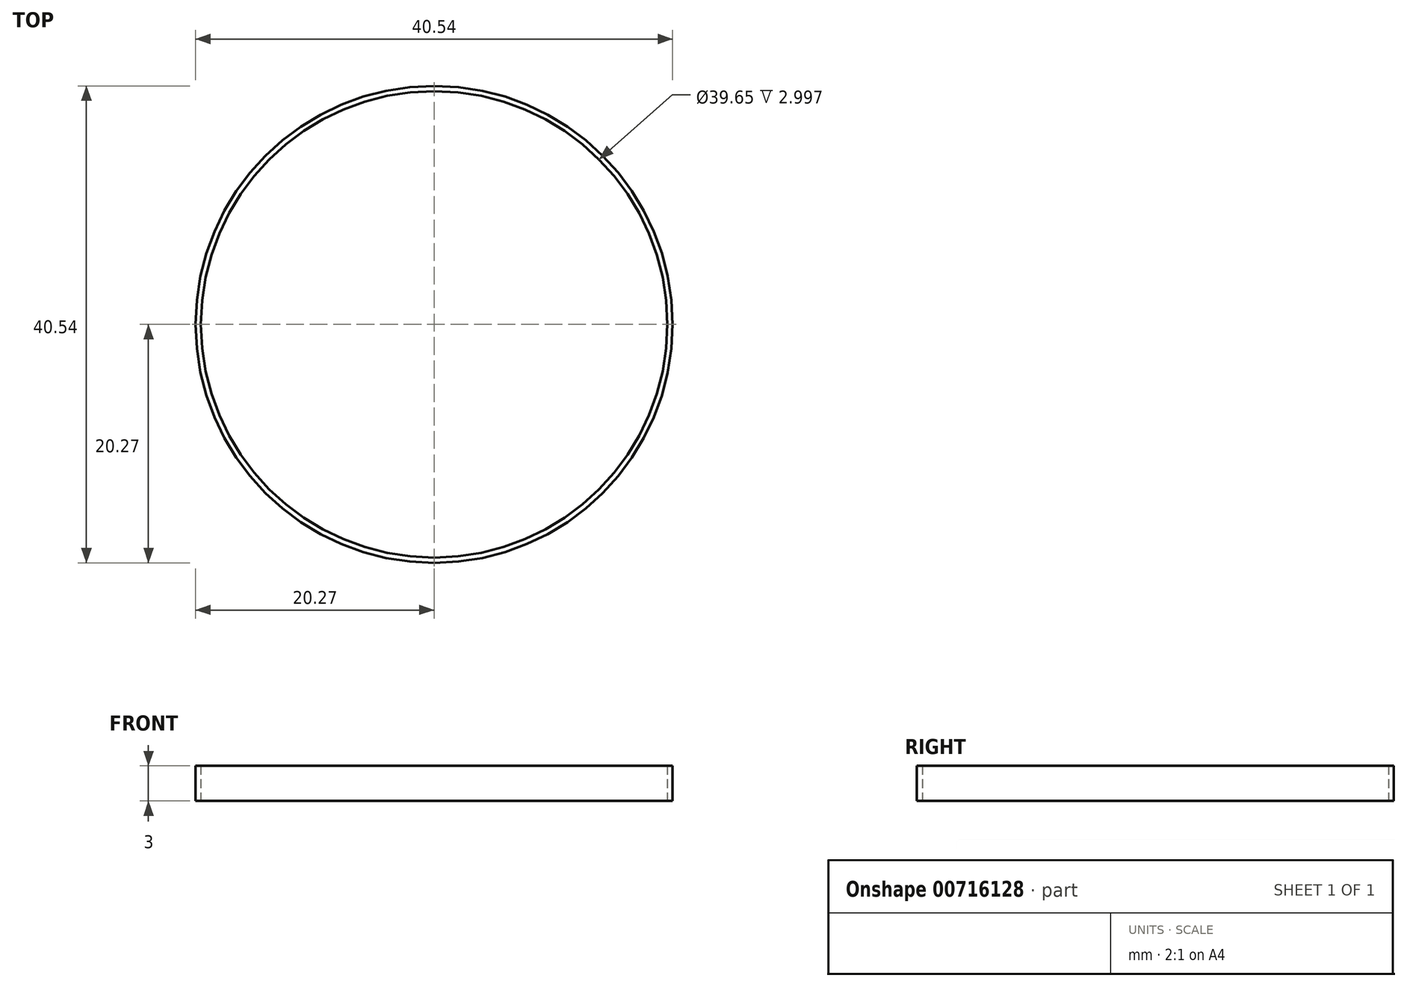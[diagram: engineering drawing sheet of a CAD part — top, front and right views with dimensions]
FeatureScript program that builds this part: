
annotation { "Feature Type Name" : "Feature", "Feature Type Description" : "" }
export const myFeature = defineFeature(function(context is Context, id is Id, definition is map)
    precondition{}
    {
        {
            var Q0;
            Q0=qCreatedBy(makeId("Top.planeOp"),FACE);
            var sketch = newSketch(context, id + "F0", { "sketchPlane" : qUnion([Q0])});
            skCircle(sketch, "E0", {"center": v(0, 0) * mm, "radius": 19.82 * mm});
            skCircle(sketch, "E1", {"center": v(0, 0) * mm, "radius": 20.27 * mm});
            skSolve(sketch);
        }
        {
            var Q0;
            Q0=makeQuery(id+"F0.imprint","IMPRINT",FACE,{"disambiguationData":[TD([[makeQuery(id+"F0.imprint","IMPRINT",EDGE,{"derivedFrom":sQuery(id+"F0.wireOp",EDGE,"E0")}),-1.0]])]});
            extrude(context, id + "F1", {"entities" : qUnion([Q0]), "depth" : 3 * mm, "offsetDistance" : 25.4 * mm});
        }
    });
